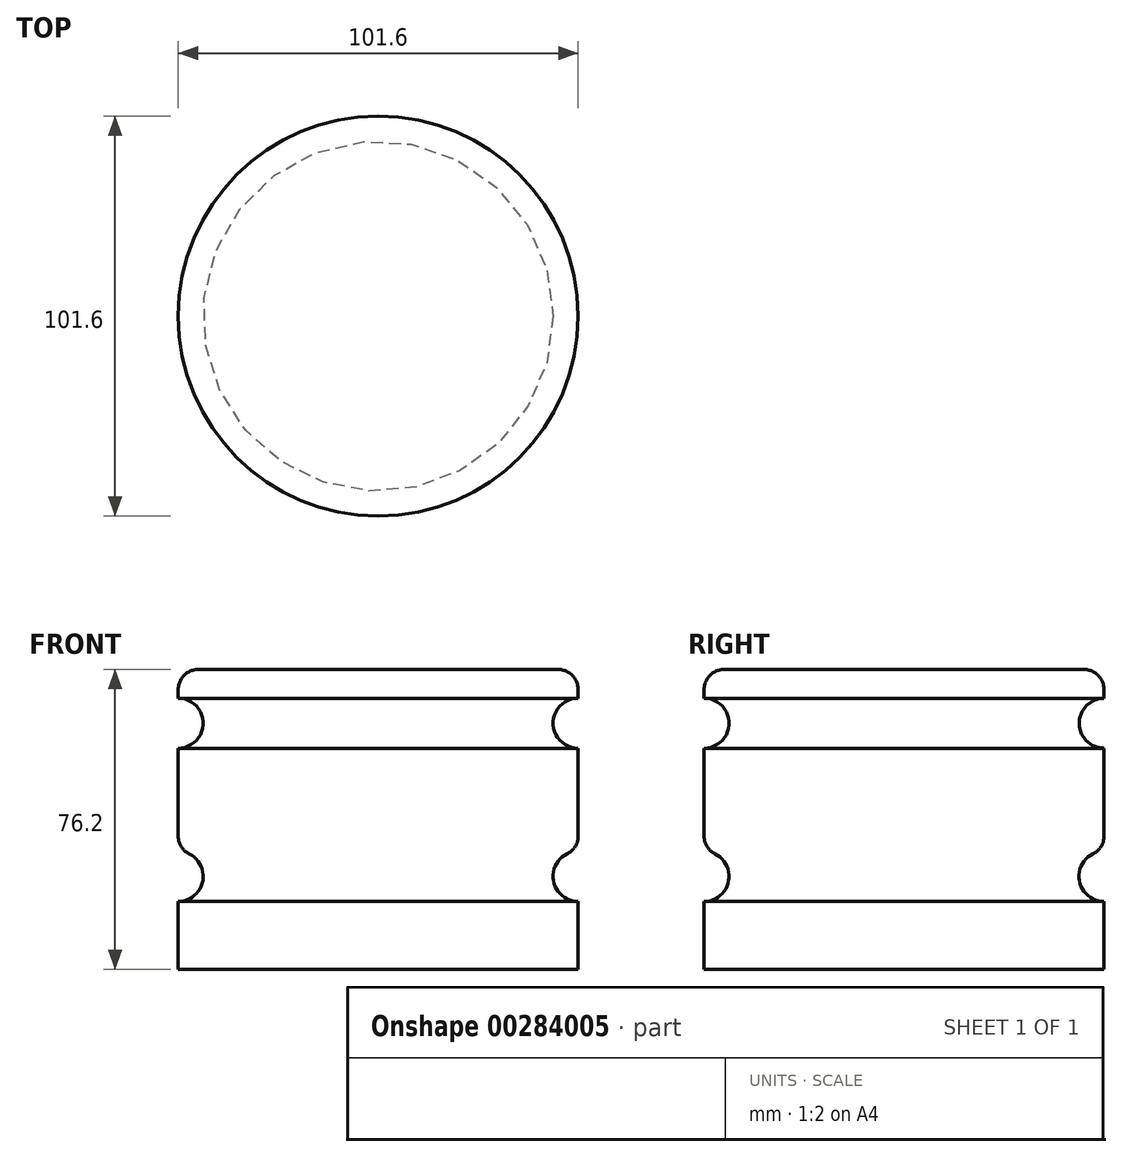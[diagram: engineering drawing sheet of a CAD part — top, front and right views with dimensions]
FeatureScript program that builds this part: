
annotation { "Feature Type Name" : "Feature", "Feature Type Description" : "" }
export const myFeature = defineFeature(function(context is Context, id is Id, definition is map)
    precondition{}
    {
        {
            var Q0;
            Q0=qCreatedBy(makeId("Front.planeOp"),FACE);
            var sketch = newSketch(context, id + "F0", { "sketchPlane" : qUnion([Q0])});
            skLineSegment(sketch, "E0", {"start": v(-49.84, 104.08) * mm, "end": v(-49.84, 27.88) * mm});
            skLineSegment(sketch, "E1", {"start": v(-49.84, 27.88) * mm, "end": v(0.96, 27.88) * mm});
            skLineSegment(sketch, "E2", {"start": v(0.96, 27.88) * mm, "end": v(0.96, 104.08) * mm});
            skLineSegment(sketch, "E3", {"start": v(0.96, 104.08) * mm, "end": v(-49.84, 104.08) * mm});
            skCircle(sketch, "E4", {"center": v(0.96, 90.44) * mm, "radius": 6.35 * mm});
            skCircle(sketch, "E5", {"center": v(0.96, 51.52) * mm, "radius": 6.35 * mm});
            skSolve(sketch);
        }
        {
            var Q0;
            Q0=makeQuery(id+"F0.imprint","IMPRINT",FACE,{"disambiguationData":[TD([[makeQuery(id+"F0.imprint","IMPRINT",EDGE,{"derivedFrom":sQuery(id+"F0.wireOp",EDGE,"E0")}),1.0]])]});
            var Q1;
            Q1=sQuery(id+"F0.wireOp",EDGE,"E0");
            revolve(context, id + "F1", {"entities" : qUnion([Q0]), "axis" : qUnion([Q1]), "revolveType" : RevolveType.FULL});
        }
        {
            var Q0;
            Q0=makeQuery(id+"F1.opRevolve","SWEPT_EDGE",EDGE,{"disambiguationData":[OSD([sQuery(id+"F0.wireOp",EDGE,"E2"),sQuery(id+"F0.wireOp",EDGE,"E3")])]});
            var Q1;
            {var subQ0=sQuery(id+"F0.wireOp",EDGE,"E5");var subQ1=sQuery(id+"F0.wireOp",EDGE,"E2");Q1=makeQuery(id+"F1.opRevolve","SWEPT_EDGE",EDGE,{"disambiguationData":[OSD([subQ1,subQ0]),TDD([makeQuery(id+"F0.imprint","INTERSECT",VERTEX,{"disambiguationData":[OD(0.0)],"derivedFrom":[subQ1,subQ0]})])]});}
            fillet(context, id + "F2", {"entities" : qUnion([Q0, Q1]), "radius" : 5.08 * mm, "tangentPropagation" : true, "allowEdgeOverflow" : false});
        }
    });
